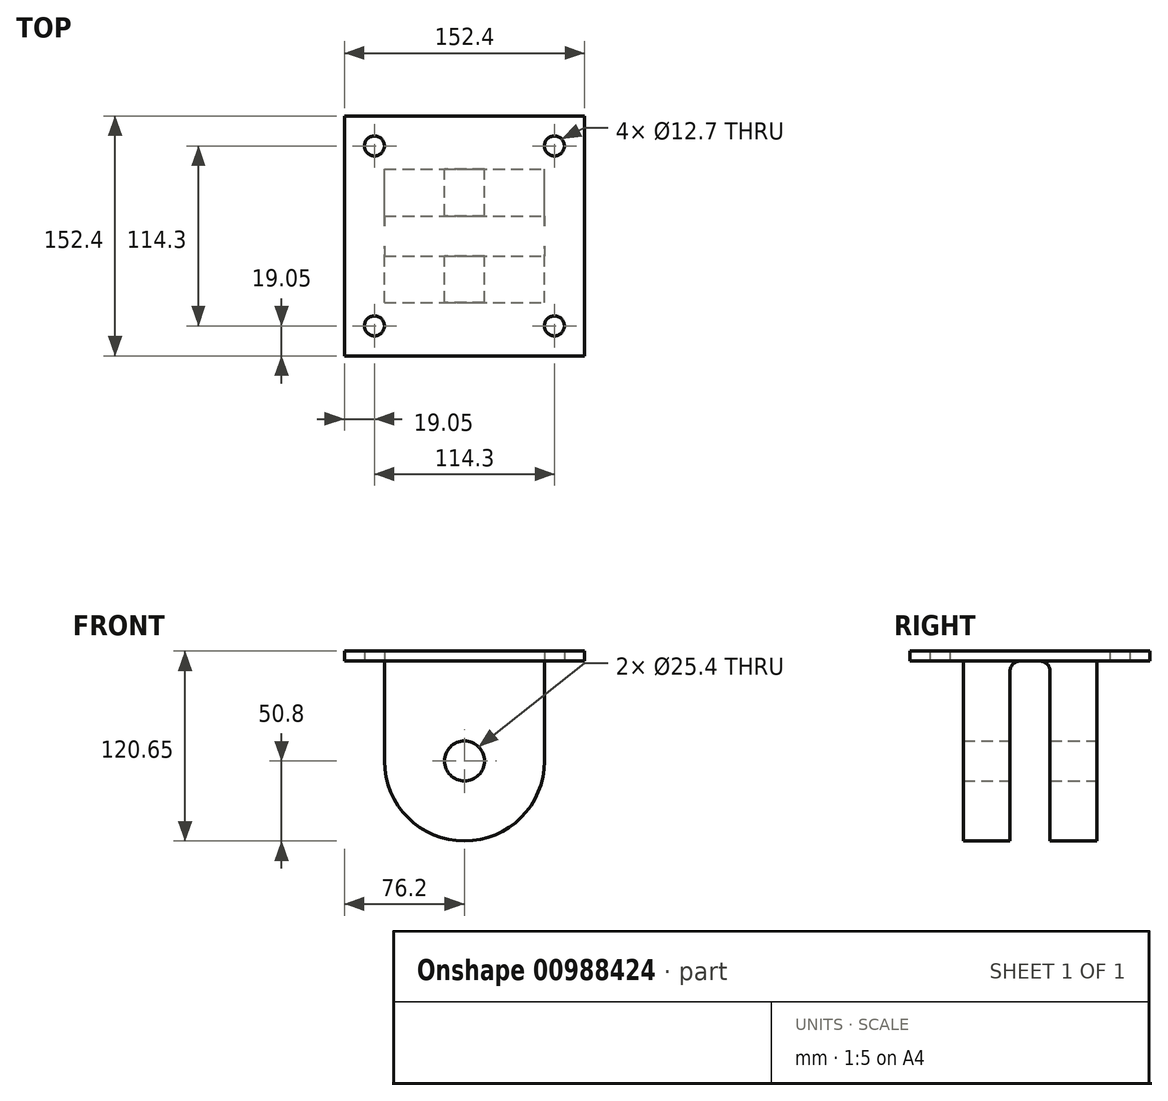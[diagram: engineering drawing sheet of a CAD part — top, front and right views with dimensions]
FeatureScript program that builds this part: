
annotation { "Feature Type Name" : "Feature", "Feature Type Description" : "" }
export const myFeature = defineFeature(function(context is Context, id is Id, definition is map)
    precondition{}
    {
        {
            assignVariable(context, id + "F0", {"name" : "FlangeWidth", "anyValue" : 29.74 * mm});
        }
        {
            assignVariable(context, id + "F1", {"name" : "FittingEyeBoltThickness", "anyValue" : 25.4 * mm});
        }
        {
            var Q0;
            Q0=qCreatedBy(makeId("Top.planeOp"),FACE);
            var sketch = newSketch(context, id + "F2", { "sketchPlane" : qUnion([Q0])});
            skLineSegment(sketch, "E0.bottom", {"start": v(76.2, -76.2) * mm, "end": v(-76.2, -76.2) * mm});
            skLineSegment(sketch, "E0.top", {"start": v(76.2, 76.2) * mm, "end": v(-76.2, 76.2) * mm});
            skLineSegment(sketch, "E0.left", {"start": v(76.2, -76.2) * mm, "end": v(76.2, 76.2) * mm});
            skLineSegment(sketch, "E0.right", {"start": v(-76.2, -76.2) * mm, "end": v(-76.2, 76.2) * mm});
            skPoint(sketch, "E0.middle", {"position": v(0, 0) * mm});
            skCircle(sketch, "E1", {"center": v(-57.15, -57.15) * mm, "radius": 6.35 * mm});
            skCircle(sketch, "E2", {"center": v(57.15, -57.15) * mm, "radius": 6.35 * mm});
            skCircle(sketch, "E3", {"center": v(-57.15, 57.15) * mm, "radius": 6.35 * mm});
            skCircle(sketch, "E4", {"center": v(57.15, 57.15) * mm, "radius": 6.35 * mm});
            skSolve(sketch);
        }
        {
            var Q0;
            Q0 = qSketchRegion(id + "F2", true);
            extrude(context, id + "F3", {"entities" : qUnion([Q0]), "depth" : 6.35 * mm, "offsetDistance" : 25.4 * mm});
        }
        {
            var Q0;
            Q0=qCreatedBy(makeId("Front.planeOp"),FACE);
            var sketch = newSketch(context, id + "F4", { "sketchPlane" : qUnion([Q0])});
            skLineSegment(sketch, "E5", {"start": v(-50.8, 0) * mm, "end": v(-50.8, -63.5) * mm});
            skLineSegment(sketch, "E6", {"start": v(50.8, 0) * mm, "end": v(50.8, -63.5) * mm});
            skLineSegment(sketch, "E7", {"start": v(-50.8, 0) * mm, "end": v(50.8, 0) * mm});
            skArc(sketch, "E8", {"start": v(-50.8, -63.5) * mm, "mid": v(0, -114.3) * mm, "end": v(50.8, -63.5) * mm});
            skCircle(sketch, "E9", {"center": v(0, -63.5) * mm, "radius": 12.7 * mm});
            skSolve(sketch);
        }
        {
            var Q0;
            Q0=makeQuery(id+"F4.imprint","IMPRINT",FACE,{"disambiguationData":[TD([[makeQuery(id+"F4.imprint","IMPRINT",EDGE,{"derivedFrom":sQuery(id+"F4.wireOp",EDGE,"E5")}),1.0]])]});
            extrude(context, id + "F5", {"entities" : qUnion([Q0]), "operationType" : NewBodyOperationType.ADD, "depth" : getVariable(context, 'FlangeWidth') * 2 + getVariable(context, 'FittingEyeBoltThickness'), "offsetDistance" : 25.4 * mm, "symmetric" : true});
        }
        {
            var Q0;
            Q0=qCreatedBy(makeId("Front.planeOp"),FACE);
            var sketch = newSketch(context, id + "F6", { "sketchPlane" : qUnion([Q0])});
            skLineSegment(sketch, "E10.bottom", {"start": v(-76.89, 0) * mm, "end": v(75.51, 0) * mm});
            skLineSegment(sketch, "E10.top", {"start": v(-76.89, -139.7) * mm, "end": v(75.51, -139.7) * mm});
            skLineSegment(sketch, "E10.left", {"start": v(-76.89, 0) * mm, "end": v(-76.89, -139.7) * mm});
            skLineSegment(sketch, "E10.right", {"start": v(75.51, 0) * mm, "end": v(75.51, -139.7) * mm});
            skSolve(sketch);
        }
        {
            var Q0;
            Q0 = qSketchRegion(id + "F6", true);
            extrude(context, id + "F7", {"entities" : qUnion([Q0]), "operationType" : NewBodyOperationType.REMOVE, "depth" : getVariable(context, 'FittingEyeBoltThickness'), "offsetDistance" : 25.4 * mm, "symmetric" : true});
        }
        {
            var Q0;
            Q0=makeQuery(id+"F5.opExtrude","CAP_EDGE",EDGE,{"disambiguationData":[OSD([sQuery(id+"F4.wireOp",EDGE,"E7")])],"isStart":true});
            var Q1;
            {var subQ0=sQuery(id+"F6.wireOp",EDGE,"E10.bottom");var subQ1=sQuery(id+"F4.wireOp",EDGE,"E7");var subQ2=sQuery(id+"F4.wireOp",EDGE,"E5");Q1=makeQuery(id+"F7.boolean.opBoolean","SPLIT",EDGE,{"disambiguationData":[TD([makeQuery(id+"F7.opExtrude","CAP_FACE",FACE,{"disambiguationData":[OSD([subQ0,sQuery(id+"F6.wireOp",EDGE,"E10.top"),sQuery(id+"F6.wireOp",EDGE,"E10.left"),sQuery(id+"F6.wireOp",EDGE,"E10.right")])],"isStart":true})])],"derivedFrom":makeQuery(id+"F5.opExtrude","SWEPT_EDGE",EDGE,{"disambiguationData":[OSD([subQ2,subQ1])]})});}
            var Q2;
            {var subQ0=sQuery(id+"F6.wireOp",EDGE,"E10.bottom");var subQ1=sQuery(id+"F4.wireOp",EDGE,"E5");var subQ2=sQuery(id+"F4.wireOp",EDGE,"E7");Q2=makeQuery(id+"F7.boolean.opBoolean","SPLIT",EDGE,{"disambiguationData":[TD([makeQuery(id+"F7.opExtrude","CAP_FACE",FACE,{"disambiguationData":[OSD([subQ0,sQuery(id+"F6.wireOp",EDGE,"E10.top"),sQuery(id+"F6.wireOp",EDGE,"E10.left"),sQuery(id+"F6.wireOp",EDGE,"E10.right")])],"isStart":false})])],"derivedFrom":makeQuery(id+"F5.opExtrude","SWEPT_EDGE",EDGE,{"disambiguationData":[OSD([subQ1,subQ2])]})});}
            var Q3;
            Q3=makeQuery(id+"F7.boolean.opBoolean","COPY",EDGE,{"derivedFrom":makeQuery(id+"F7.opExtrude","CAP_EDGE",EDGE,{"disambiguationData":[OSD([sQuery(id+"F6.wireOp",EDGE,"E10.bottom")])],"isStart":false})});
            var Q4;
            Q4=makeQuery(id+"F7.boolean.opBoolean","COPY",EDGE,{"derivedFrom":makeQuery(id+"F7.opExtrude","CAP_EDGE",EDGE,{"disambiguationData":[OSD([sQuery(id+"F6.wireOp",EDGE,"E10.bottom")])],"isStart":true})});
            var Q5;
            Q5=makeQuery(id+"F5.opExtrude","CAP_EDGE",EDGE,{"disambiguationData":[OSD([sQuery(id+"F4.wireOp",EDGE,"E7")])],"isStart":false});
            var Q6;
            {var subQ0=sQuery(id+"F6.wireOp",EDGE,"E10.bottom");var subQ1=sQuery(id+"F4.wireOp",EDGE,"E6");var subQ2=sQuery(id+"F4.wireOp",EDGE,"E7");Q6=makeQuery(id+"F7.boolean.opBoolean","SPLIT",EDGE,{"disambiguationData":[TD([makeQuery(id+"F7.opExtrude","CAP_FACE",FACE,{"disambiguationData":[OSD([subQ0,sQuery(id+"F6.wireOp",EDGE,"E10.top"),sQuery(id+"F6.wireOp",EDGE,"E10.left"),sQuery(id+"F6.wireOp",EDGE,"E10.right")])],"isStart":true})])],"derivedFrom":makeQuery(id+"F5.opExtrude","SWEPT_EDGE",EDGE,{"disambiguationData":[OSD([subQ1,subQ2])]})});}
            var Q7;
            {var subQ0=sQuery(id+"F6.wireOp",EDGE,"E10.bottom");var subQ1=sQuery(id+"F4.wireOp",EDGE,"E6");var subQ2=sQuery(id+"F4.wireOp",EDGE,"E7");Q7=makeQuery(id+"F7.boolean.opBoolean","SPLIT",EDGE,{"disambiguationData":[TD([makeQuery(id+"F7.opExtrude","CAP_FACE",FACE,{"disambiguationData":[OSD([subQ0,sQuery(id+"F6.wireOp",EDGE,"E10.top"),sQuery(id+"F6.wireOp",EDGE,"E10.left"),sQuery(id+"F6.wireOp",EDGE,"E10.right")])],"isStart":false})])],"derivedFrom":makeQuery(id+"F5.opExtrude","SWEPT_EDGE",EDGE,{"disambiguationData":[OSD([subQ1,subQ2])]})});}
            fillet(context, id + "F8", {"entities" : qUnion([Q0, Q1, Q2, Q3, Q4, Q5, Q6, Q7]), "radius" : 6.35 * mm, "tangentPropagation" : true, "allowEdgeOverflow" : false});
        }
    });
